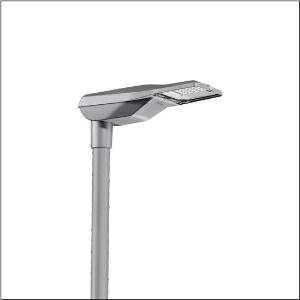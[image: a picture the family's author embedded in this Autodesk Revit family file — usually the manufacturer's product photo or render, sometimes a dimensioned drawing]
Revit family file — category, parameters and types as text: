
# Revit family: streetlight_sl_21_iq_micro___st1_0ab_5xe1m31g08db_d575
name_source: partatom
category: Lighting Fixtures
units: mm (PartAtom-declared; Revit-internal decimal feet)

## family parameters
Cut with Voids When Loaded = No
Host = Face
Light Source = No
Part Type = Normal
Room Calculation Point = No
Round Connector Dimension = Use Diameter
Shared = No

## types (1)
- --- (1 x LED, 4240 lm, 36.4 W, 3000K)
    Apparent Load = 36 VA
    CIE Flux Codes = 38 73 97 100 100
    Color Rendering = 70
    Color Temperature = 3000K
    Default Elevation = 1800 mm
    Description = Streetlight SL 21 iQ micro, mast luminaire, primary light control with lens, of PMMA, primary optical cover: cover, of toughened safety glass, transparent, light distribution: ST1.0aB, light emission: direct distribution, primary light characteristic: asymmetric, installation type: post-top, side-entry, LED, High Power LED, rated luminous flux: 4.240lm, luminous efficacy: 117lm/W, light colour: 730, colour temperature: 3000K, control: Street-Remote, Auto-Match, Temp-Guard, Lumen-Switch, Night-Set, Smart-Wire, Light-Fading, Desk-Remote (wireless, voltage-free reading and setting of iQ features in the workshop via application-optimized NFC function/RFID function), optimised constant luminous flux control (CLO 2.0), presetting dimming linear, mains connection: 220..240V, AC, 50/60Hz, start of lifetime: 36W, end of service life: 38W, reduction: 16W, luminaire housing, of diecast aluminium, powder-coated, Siteco® metallic grey (DB 702S), corrosivity category C5 mid according to DIN EN ISO 12944, please order mast flange separately, inclination adjustable: 0°, 5°, 10°, 15°, sealing non-destructively replaceable, multi-level sealing system, length: 528mm, width: 235mm, height: 110mm, mast flange for spigot size: 42mm (side-entry): 5XC10008XM4, 60/48mm (side-entry/post-top): 5XC10108XM2, 76/60mm (side-entry/post-top): 5XC10108XM1, protection rating (complete): IP66, insulation class (complete): insulation class II (safety insulation), certification: CE, ENEC, ENEC+, VDE, impact resistance: IK09, permissible operating ambient temperature for outdoor applications: -40..+50°C, standard-compliant lighting for roads and squares, packaging unit: 1 piece

Light Distribution: ST1.0aB
    Height = 110 mm
    Lamp = 1 x LED
    Lamp Light Flux = 4240 lm
    Lamp Power = 36.4 W
    Lamp count = 1
    Length = 528 mm
    Luminous efficacy = 116 lm/W
    Manufacturer = Siteco
    ModVariant = No
    Model = 5XE1M31G08DB
    Number of Poles = 1
    OnlyDefault = Yes
    Power Factor = 1
    Product Name = Streetlight SL 21 iQ micro | ST1.0aB
    Product group = mast luminaire | pylon top
    ProductGroupID = 6100
    Protection Class = Protection class II
    Protection Degree = IP 66
    RLX_Detail_Level = 1
    RLX_Emergency_Light_Flux = 0 lm
    RLX_Emergency_Type = 0
    RLX_Emergency_Type_DB = No
    RlxData = <blob elided: 99181 chars, md5=b21a7bbc>
    Socket = socket
    Standby Power = 0 W
    System Light Flux = 4240 lm
    System Power = 36 W
    Type Comments = factory setting: luminous flux: 100 % | dim-lin: 254 | 715 mA
    Type Image = l_1006881.jpg
    URL = http://relux.com
    VarID = @adj_086357
    Voltage = 0 V
    Weight = 0.00 kg
    Width = 235 mm

## geometry (parser evidence)
native form markers: Blend x4, Sweep x10
no freeform markers — native parametric forms only
